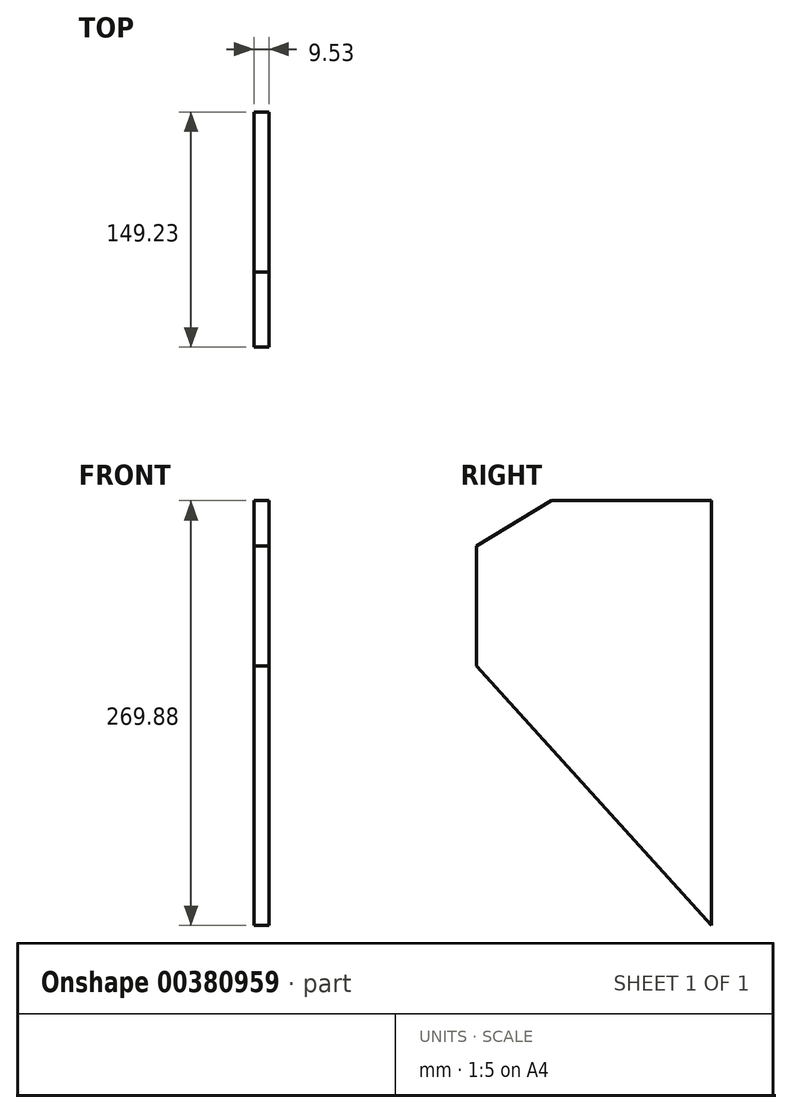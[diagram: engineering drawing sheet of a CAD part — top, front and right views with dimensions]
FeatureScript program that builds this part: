
annotation { "Feature Type Name" : "Feature", "Feature Type Description" : "" }
export const myFeature = defineFeature(function(context is Context, id is Id, definition is map)
    precondition{}
    {
        {
            var Q0;
            Q0=qCreatedBy(makeId("Right.planeOp"),FACE);
            var sketch = newSketch(context, id + "F0", { "sketchPlane" : qUnion([Q0])});
            skLineSegment(sketch, "E0", {"start": v(0, 0) * mm, "end": v(0, 269.88) * mm});
            skLineSegment(sketch, "E1", {"start": v(0, 269.88) * mm, "end": v(-101.6, 269.88) * mm});
            skLineSegment(sketch, "E2", {"start": v(-101.6, 269.88) * mm, "end": v(-149.23, 240.9) * mm});
            skLineSegment(sketch, "E3", {"start": v(-149.23, 240.9) * mm, "end": v(-149.23, 164.7) * mm});
            skLineSegment(sketch, "E4", {"start": v(-149.23, 164.7) * mm, "end": v(0, 0) * mm});
            skSolve(sketch);
        }
        {
            var Q0;
            Q0=qSketchRegion(id+"F0",true);
            extrude(context, id + "F1", {"entities" : qUnion([Q0]), "depth" : 9.52 * mm});
        }
    });
